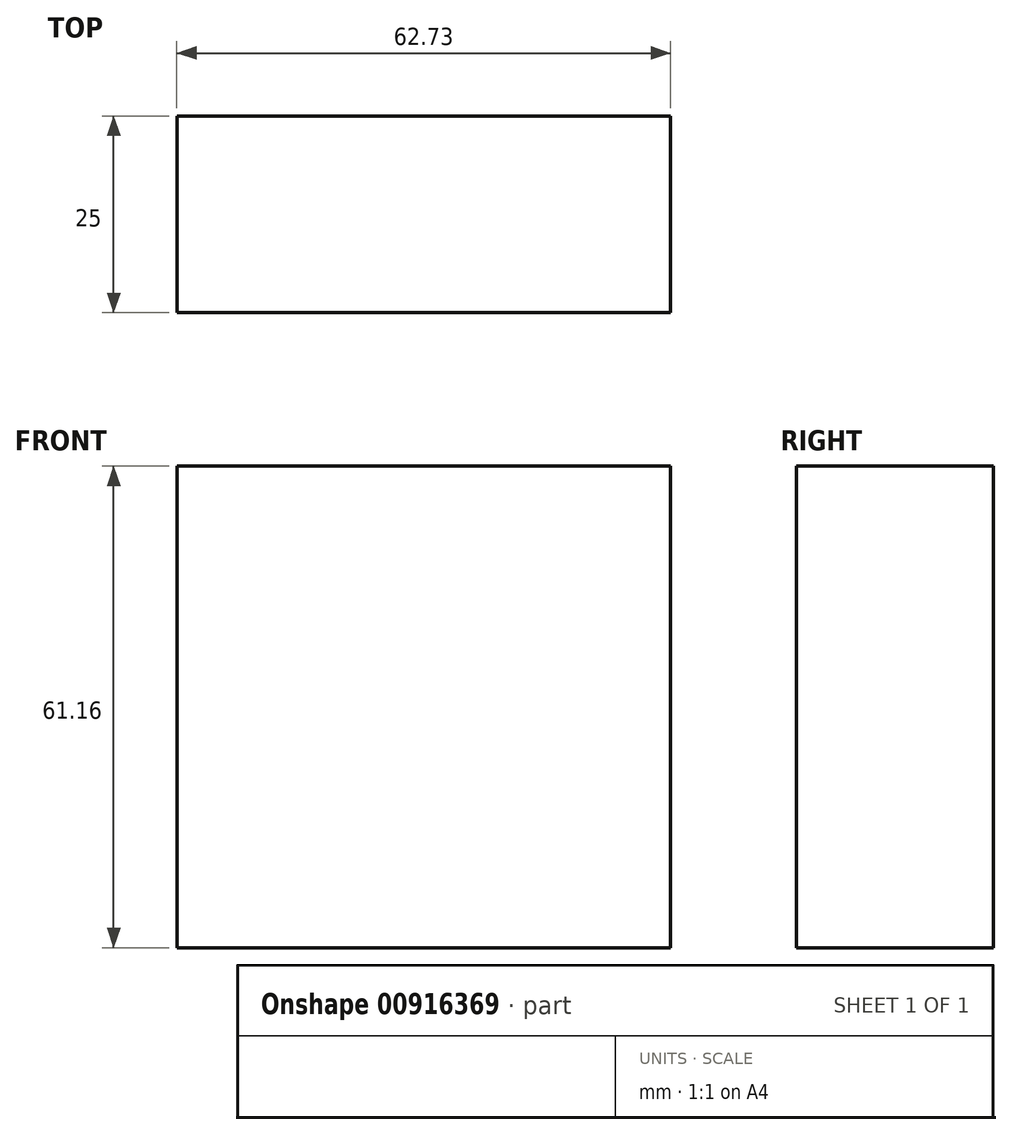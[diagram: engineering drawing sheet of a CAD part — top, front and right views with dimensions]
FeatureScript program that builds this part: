
annotation { "Feature Type Name" : "Feature", "Feature Type Description" : "" }
export const myFeature = defineFeature(function(context is Context, id is Id, definition is map)
    precondition{}
    {
        {
            var Q0;
            Q0=qCreatedBy(makeId("Front.planeOp"),FACE);
            var sketch = newSketch(context, id + "F0", { "sketchPlane" : qUnion([Q0])});
            skLineSegment(sketch, "E0.bottom", {"start": v(-99.66, 32.68) * mm, "end": v(-36.93, 32.68) * mm});
            skLineSegment(sketch, "E0.top", {"start": v(-99.66, -28.48) * mm, "end": v(-36.93, -28.48) * mm});
            skLineSegment(sketch, "E0.left", {"start": v(-99.66, 32.68) * mm, "end": v(-99.66, -28.48) * mm});
            skLineSegment(sketch, "E0.right", {"start": v(-36.93, 32.68) * mm, "end": v(-36.93, -28.48) * mm});
            skSolve(sketch);
        }
        {
            var Q0;
            Q0 = qSketchRegion(id + "F0", true);
            extrude(context, id + "F1", {"entities" : qUnion([Q0]), "depth" : 25 * mm, "offsetDistance" : 25 * mm});
        }
    });
